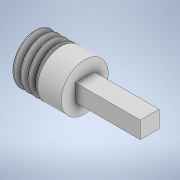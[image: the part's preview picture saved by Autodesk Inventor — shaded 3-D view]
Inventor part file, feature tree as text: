
AUTODESK INVENTOR PART (.ipt)
format: ipt  version: 2020 (Build 240168000, 168)  size: 438,784 bytes
history: native  units: mm
features: sketch x5, extrude x2, revolve x2, thread x1, helix x1
ambient origin geometry x8: Origin, YZ Plane, XZ Plane, XY Plane, X Axis, Y Axis, Z Axis, Center Point
bodies: Solid1 (feature_tree), Solid2 (feature_tree)
feature tree (11):
  extrude  "Extrusion1"  Depth=5.5mm TaperAngle=0.0deg
  thread  "Thread1"  [1 undecoded]
  revolve  "Revolution1"  [1 undecoded]
  revolve  "Revolution2"  [1 undecoded]
  helix  "Coil1"  [1 undecoded]
  extrude  "Extrusion5"  Depth=0.8008mm
  sketch  "Sketch1"  dims[d0=5.0mm d1=5.5mm d2=0.0mm d3=3.0mm d4=0.0mm]
  sketch  "Sketch3"  dims[d8=9.599311mm d9=0.128066mm d10=0.128066mm d13=0.8mm]
  sketch  "Sketch4"  dims[d15=9.599311mm d17=0.0mm d18=0.0mm]
  sketch  "Sketch5"  dims[d19=0.8008mm d20=4.6mm d21=10.0mm d22=0.0mm d23=0.0mm d24=0.0mm d25=0.0mm d26=0.0mm d38=9.599311mm]
  sketch  "Sketch20"  dims[d64=9.599311mm d85=9.599311mm d106=9.599311mm d121=1.0mm d122=0.9mm d123=1.0mm d124=0.9mm d125=1.0mm d126=0.9mm d127=6.9mm d128=0.0mm d129=0.9mm]
note: 4 required parameter values undecoded (feature->parameter linkage not recoverable at this tier; creation-order binding heuristic only, values carry confidence <= 0.55)